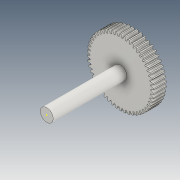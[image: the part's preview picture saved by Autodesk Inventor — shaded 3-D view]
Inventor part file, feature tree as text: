
AUTODESK INVENTOR PART (.ipt)
format: ipt  version: 2021 (Build 250183000, 183)  size: 341,504 bytes
history: native  units: mm (DEFAULTED — no unit token found)
features: sketch x5, plane x3, other x3, extrude x2
ambient origin geometry x8: Origin, YZ Plane, XZ Plane, XY Plane, X Axis, Y Axis, Z Axis, Center Point
bodies: Solid1 (feature_tree)
feature tree (13):
  extrude  "Extrusion1"  Depth=2.0mm TaperAngle=0.0deg
  plane  "Work Plane2"
  plane  "Work Plane8"
  plane  "Work Plane9"
  other  "Engrenagem reta"
  extrude  "Extrusão2"  Depth=10.0mm TaperAngle=0.0deg
  sketch  "Esboço4"  dims[d17=0.0mm d34=0.628319mm]
  sketch  "Esboço5"  dims[d39=0.0mm d41=0.0mm d43=10.7mm d46=10.7mm d47=0.0mm d48=0.0mm d49=11.5mm d50=0.0mm d51=0.5mm d52=0.872665mm]
  sketch  "Sketch1"  dims[d0=10.4mm d1=2.0mm d2=0.0mm]
  sketch  "Sketch2"  dims[d3=10.0mm d4=10.0mm d5=0.0mm]
  other  "Srf1"
  sketch  "Esboço3"  dims[d16=10.7mm]
  other  "Diâmetro do flanco"
